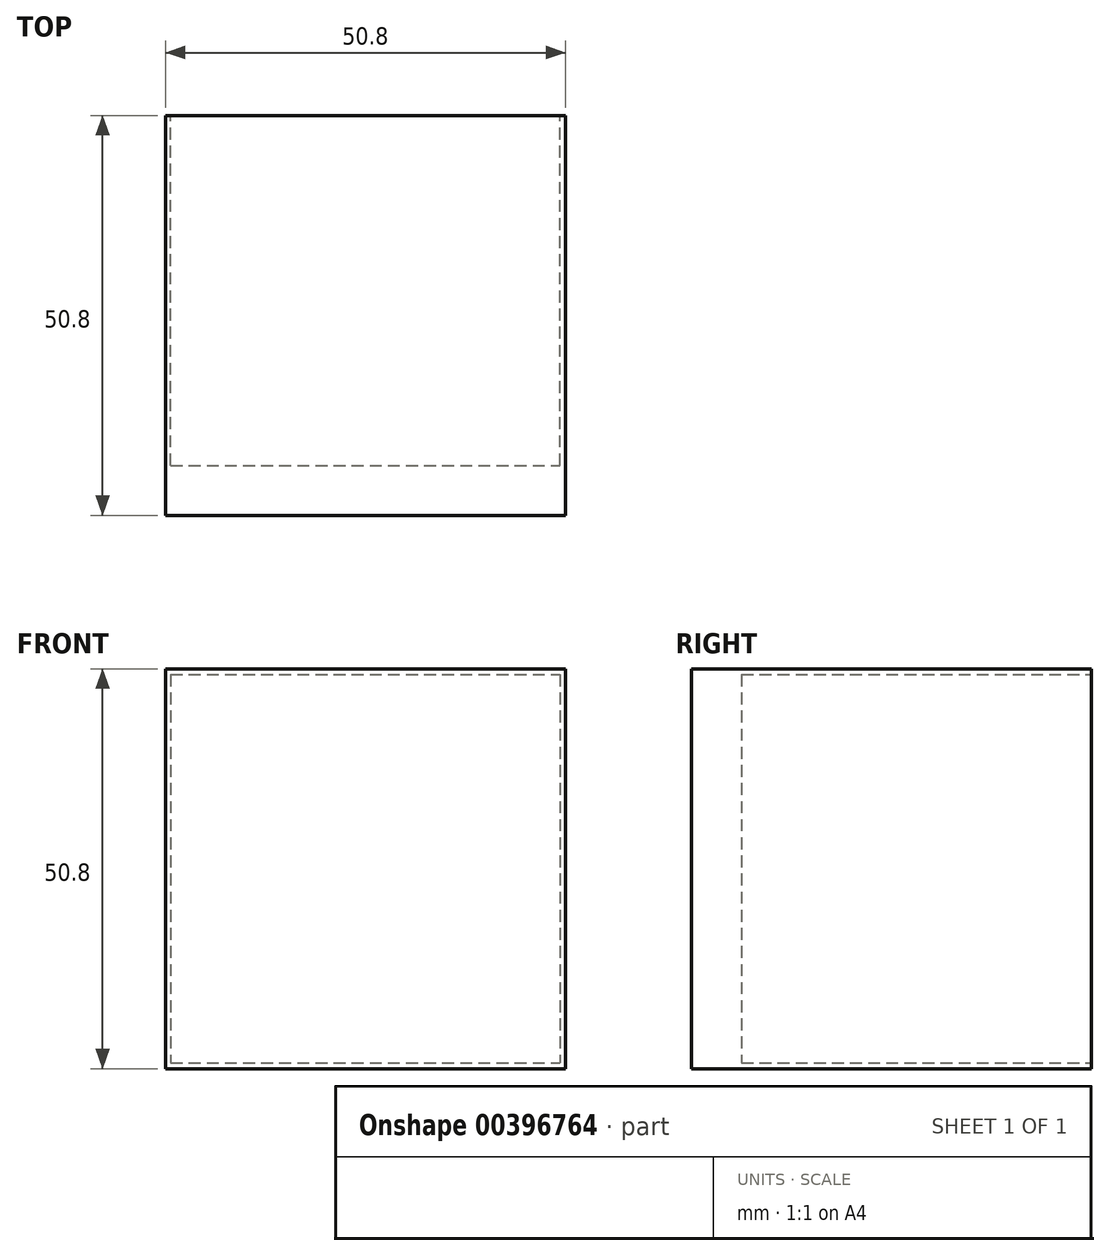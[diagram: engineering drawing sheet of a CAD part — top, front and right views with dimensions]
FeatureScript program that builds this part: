
annotation { "Feature Type Name" : "Feature", "Feature Type Description" : "" }
export const myFeature = defineFeature(function(context is Context, id is Id, definition is map)
    precondition{}
    {
        {
            var Q0;
            Q0=qCreatedBy(makeId("Front.planeOp"),FACE);
            var sketch = newSketch(context, id + "F0", { "sketchPlane" : qUnion([Q0])});
            skLineSegment(sketch, "E0.bottom", {"start": v(0, 0) * mm, "end": v(50.8, 0) * mm});
            skLineSegment(sketch, "E0.top", {"start": v(0, 50.8) * mm, "end": v(50.8, 50.8) * mm});
            skLineSegment(sketch, "E0.left", {"start": v(0, 0) * mm, "end": v(0, 50.8) * mm});
            skLineSegment(sketch, "E0.right", {"start": v(50.8, 0) * mm, "end": v(50.8, 50.8) * mm});
            skSolve(sketch);
        }
        {
            var Q0;
            Q0 = qSketchRegion(id + "F0", true);
            extrude(context, id + "F1", {"entities" : qUnion([Q0]), "depth" : 50.8 * mm});
        }
        {
            var Q0;
            Q0=makeQuery(id+"F1.opExtrude","CAP_FACE",FACE,{"disambiguationData":[OSD([sQuery(id+"F0.wireOp",EDGE,"E0.bottom"),sQuery(id+"F0.wireOp",EDGE,"E0.top"),sQuery(id+"F0.wireOp",EDGE,"E0.left"),sQuery(id+"F0.wireOp",EDGE,"E0.right")])],"isStart":true});
            var sketch = newSketch(context, id + "F2", { "sketchPlane" : qUnion([Q0])});
            skLineSegment(sketch, "E1.bottom", {"start": v(-0.64, 50.07) * mm, "end": v(-50.13, 50.07) * mm});
            skLineSegment(sketch, "E1.top", {"start": v(-0.64, 0.72) * mm, "end": v(-50.13, 0.72) * mm});
            skLineSegment(sketch, "E1.left", {"start": v(-0.64, 50.07) * mm, "end": v(-0.64, 0.72) * mm});
            skLineSegment(sketch, "E1.right", {"start": v(-50.13, 50.07) * mm, "end": v(-50.13, 0.72) * mm});
            skSolve(sketch);
        }
        {
            var Q0;
            Q0 = qSketchRegion(id + "F2", true);
            var Q1;
            Q1=makeQuery(id+"F1.opExtrude","CAP_FACE",FACE,{"disambiguationData":[OSD([sQuery(id+"F0.wireOp",EDGE,"E0.bottom"),sQuery(id+"F0.wireOp",EDGE,"E0.top"),sQuery(id+"F0.wireOp",EDGE,"E0.left"),sQuery(id+"F0.wireOp",EDGE,"E0.right")])],"isStart":false});
            extrude(context, id + "F3", {"entities" : qUnion([Q0, Q1]), "operationType" : NewBodyOperationType.ADD, "depth" : 25.4 * mm});
        }
        {
            var Q0;
            Q0=makeQuery(id+"F3.opExtrude","CAP_FACE",FACE,{"disambiguationData":[OSD([sQuery(id+"F2.wireOp",EDGE,"E1.bottom"),sQuery(id+"F2.wireOp",EDGE,"E1.top"),sQuery(id+"F2.wireOp",EDGE,"E1.left"),sQuery(id+"F2.wireOp",EDGE,"E1.right")])],"isStart":false});
            extrude(context, id + "F4", {"entities" : qUnion([Q0]), "operationType" : NewBodyOperationType.REMOVE, "oppositeDirection" : true, "depth" : 69.85 * mm});
        }
    });
